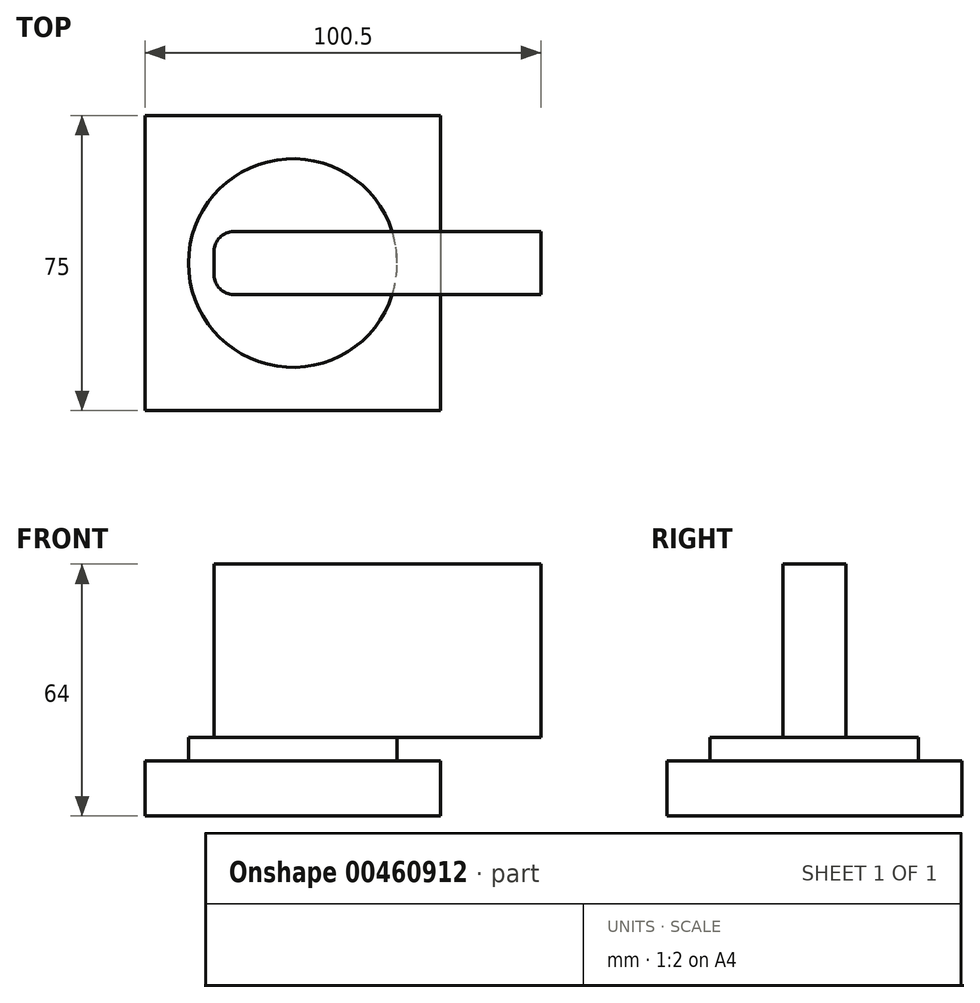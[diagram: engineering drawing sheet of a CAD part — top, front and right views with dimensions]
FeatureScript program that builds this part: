
annotation { "Feature Type Name" : "Feature", "Feature Type Description" : "" }
export const myFeature = defineFeature(function(context is Context, id is Id, definition is map)
    precondition{}
    {
        {
            var Q0;
            Q0=qCreatedBy(makeId("Top.planeOp"),FACE);
            var sketch = newSketch(context, id + "F0", { "sketchPlane" : qUnion([Q0])});
            skLineSegment(sketch, "E0.bottom", {"start": v(37.5, 37.5) * mm, "end": v(-37.5, 37.5) * mm});
            skLineSegment(sketch, "E0.top", {"start": v(37.5, -37.5) * mm, "end": v(-37.5, -37.5) * mm});
            skLineSegment(sketch, "E0.left", {"start": v(37.5, 37.5) * mm, "end": v(37.5, -37.5) * mm});
            skLineSegment(sketch, "E0.right", {"start": v(-37.5, 37.5) * mm, "end": v(-37.5, -37.5) * mm});
            skPoint(sketch, "E0.middle", {"position": v(0, 0) * mm});
            skSolve(sketch);
        }
        {
            var Q0;
            Q0 = qSketchRegion(id + "F0", true);
            extrude(context, id + "F1", {"entities" : qUnion([Q0]), "depth" : 14 * mm, "offsetDistance" : 25 * mm});
        }
        {
            var Q0;
            Q0=makeQuery(id+"F1.opExtrude","CAP_FACE",FACE,{"disambiguationData":[OSD([sQuery(id+"F0.wireOp",EDGE,"E0.bottom"),sQuery(id+"F0.wireOp",EDGE,"E0.top"),sQuery(id+"F0.wireOp",EDGE,"E0.left"),sQuery(id+"F0.wireOp",EDGE,"E0.right")])],"isStart":false});
            var sketch = newSketch(context, id + "F2", { "sketchPlane" : qUnion([Q0])});
            skCircle(sketch, "E1", {"center": v(0, 0) * mm, "radius": 26.5 * mm});
            skSolve(sketch);
        }
        {
            var Q0;
            Q0 = qSketchRegion(id + "F2", true);
            extrude(context, id + "F3", {"entities" : qUnion([Q0]), "depth" : 6 * mm, "offsetDistance" : 25 * mm});
        }
        {
            var Q0;
            Q0=makeQuery(id+"F3.opExtrude","CAP_FACE",FACE,{"disambiguationData":[OSD([sQuery(id+"F2.wireOp",EDGE,"E1")])],"isStart":false});
            var sketch = newSketch(context, id + "F4", { "sketchPlane" : qUnion([Q0])});
            skLineSegment(sketch, "E2.bottom", {"start": v(-15, 8) * mm, "end": v(63, 8) * mm});
            skLineSegment(sketch, "E2.top", {"start": v(-15, -8) * mm, "end": v(63, -8) * mm});
            skLineSegment(sketch, "E2.left", {"start": v(-20, 3) * mm, "end": v(-20, -3) * mm});
            skLineSegment(sketch, "E2.right", {"start": v(63, 8) * mm, "end": v(63, -8) * mm});
            skPoint(sketch, "E3.visualSharp", {"position": v(-20, 8) * mm});
            skArc(sketch, "E3.filletArc", {"start": v(-15, 8) * mm, "mid": v(-18.54, 6.54) * mm, "end": v(-20, 3) * mm});
            skPoint(sketch, "E4.visualSharp", {"position": v(-20, -8) * mm});
            skArc(sketch, "E4.filletArc", {"start": v(-20, -3) * mm, "mid": v(-18.54, -6.54) * mm, "end": v(-15, -8) * mm});
            skSolve(sketch);
        }
        {
            var Q0;
            Q0 = qSketchRegion(id + "F4", true);
            extrude(context, id + "F5", {"entities" : qUnion([Q0]), "operationType" : NewBodyOperationType.ADD, "depth" : 44 * mm, "offsetDistance" : 25 * mm});
        }
    });
